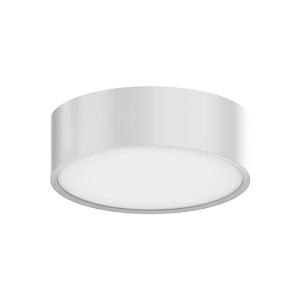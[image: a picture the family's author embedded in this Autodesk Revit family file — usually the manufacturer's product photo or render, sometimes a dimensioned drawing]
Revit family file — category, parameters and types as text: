
# Revit family: ledceilinglu-e_rd142-18w-830-wh_540001295300
name_source: partatom
category: Leuchten
revit_build: Autodesk Revit 2016 (Build: 20190508_0715(x64)
units: mm (PartAtom-declared; Revit-internal decimal feet)

## family parameters
Basisbauteil = Fläche
Beim Laden mit Abzugskörper schneiden = Nein
Bemaßung runder Anschluss = Durchmesser verwenden
Gemeinsam genutzt = Nein
Lichtquelle = Nein
Raumberechnungspunkt = Nein
Teiletyp = Normal

## types (1)
- LEDCeilingLu-E Rd142-18W-830-WH (1 x LED, 1620 lm)
    Approval mark = CE
    Beschreibung = Stylish and compact ceiling luminaire. Clean “twist-and-lock” mounting system. High quality full metal body. Low height of only 46mm. Suitable for ceiling and wall mounting.
    CIE Flux Codes = 49 80 96 100 100
    Control Gear = Electronic ballast
    Height = 100 mm  [stored 0.328084 ft]
    Hersteller = OPPLE
    Lamp Light Flux = 1620 lm
    Lamp count = 1
    Lampe = 1 x LED
    Length = 100 mm  [stored 0.328084 ft]
    Luminous efficacy = 90 lm/W
    ModVariant = Nein
    Modell = 540001295300
    Mounting Place = Wall, Ceiling
    Mounting Type = Surface mounted
    Number of Poles = 1
    OnlyDefault = Ja
    Power Factor = 1
    Product Name = LEDCeilingLu-E Rd142-18W-830-WH
    Product group = Ceiling Light Luna
    ProductGroupID = 305
    Protection Class = Protection class II
    Protection Degree = IP 20
    RLX_Detail_Level = 1
    RlxData = <blob elided: 125465 chars, md5=e559c1d2>
    Scheinlast = 18 VA
    Socket = socket
    Standby Power = 0 W
    System Light Flux = 1620 lm
    System Power = 18 W
    Typenbild = luna_wh_rd142.jpg
    Typenkommentare = Product without accessories
    URL = http://relux.com
    VarID = ---
    Voltage = 230 V
    Voltage Range = 220-240 V
    Vorgabe-Ansicht = 1800 mm
    Weight = 0.00 kg
    Width = 100 mm  [stored 0.328084 ft]

note: [stored X ft] marks values corroborated as IEEE doubles in the binary element streams (Revit-internal decimal feet)

## geometry (parser evidence)
native form markers: Blend x4, Sweep x12
no freeform markers — native parametric forms only
